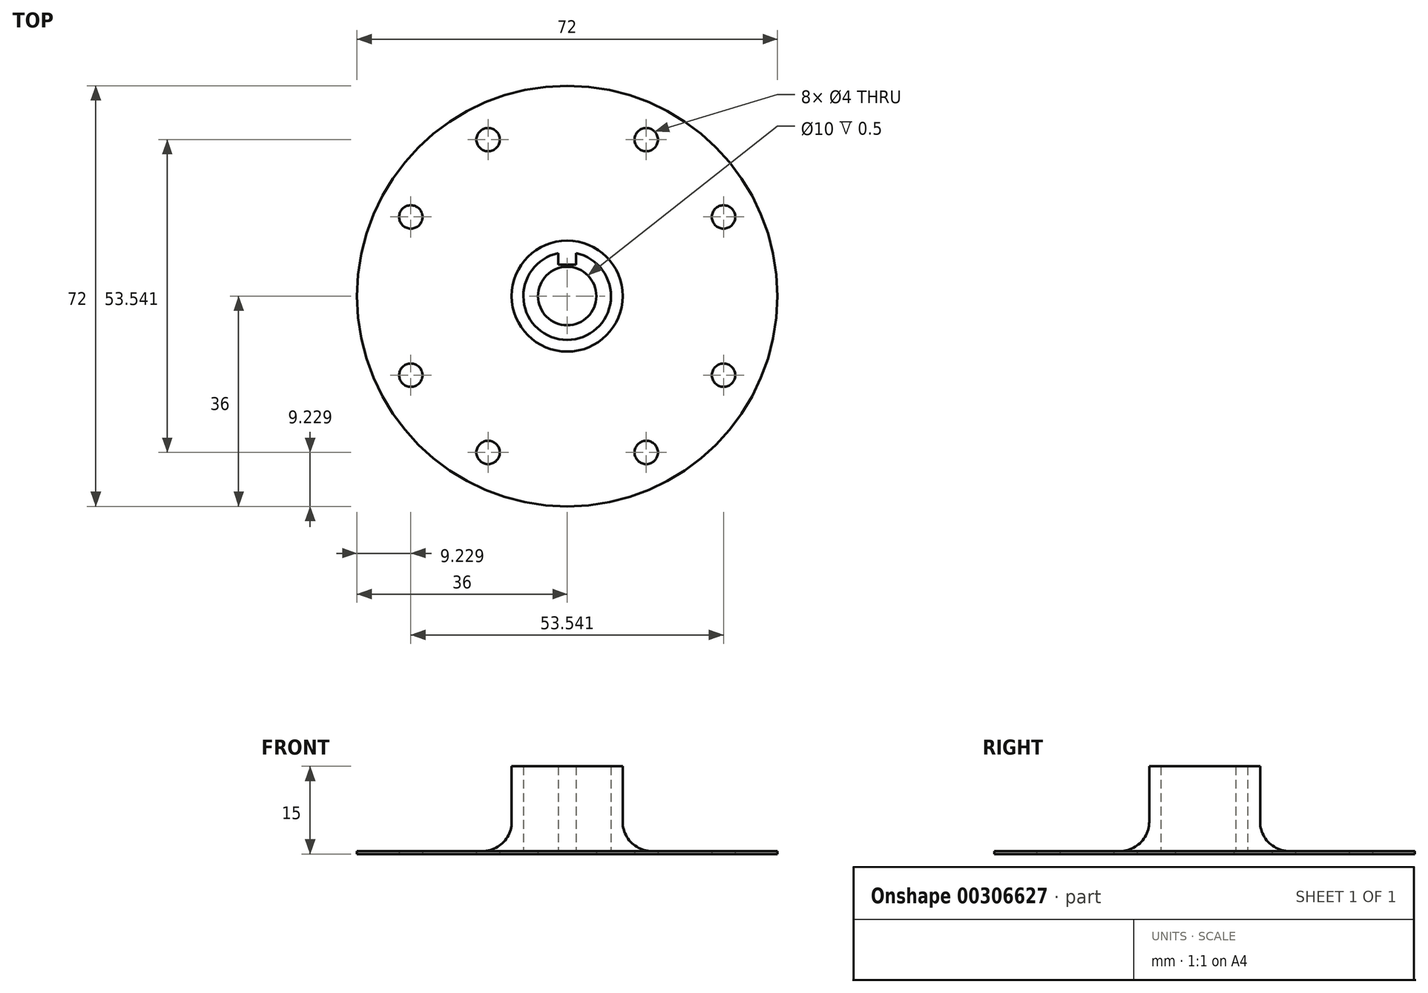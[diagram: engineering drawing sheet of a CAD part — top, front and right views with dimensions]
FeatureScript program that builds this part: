
annotation { "Feature Type Name" : "Feature", "Feature Type Description" : "" }
export const myFeature = defineFeature(function(context is Context, id is Id, definition is map)
    precondition{}
    {
        {
            assignVariable(context, id + "F0", {"name" : "Thicc", "anyValue" : .5});
        }
        {
            var Q0;
            Q0=qCreatedBy(makeId("Top.planeOp"),FACE);
            var sketch = newSketch(context, id + "F1", { "sketchPlane" : qUnion([Q0])});
            skCircle(sketch, "E0", {"center": v(0, 0) * mm, "radius": 7.5 * mm});
            skCircle(sketch, "E1", {"center": v(0, 0) * mm, "radius": 9.5 * mm});
            skLineSegment(sketch, "E2", {"start": v(-1.5, 7.35) * mm, "end": v(-1.5, 5.35) * mm});
            skLineSegment(sketch, "E3", {"start": v(-1.5, 5.35) * mm, "end": v(1.5, 5.35) * mm});
            skLineSegment(sketch, "E4", {"start": v(1.5, 5.35) * mm, "end": v(1.5, 7.35) * mm});
            skPoint(sketch, "E5", {"position": v(0, 5.35) * mm});
            skSolve(sketch);
        }
        {
            var Q0;
            Q0=qCreatedBy(makeId("Top.planeOp"),FACE);
            var sketch = newSketch(context, id + "F2", { "sketchPlane" : qUnion([Q0])});
            skCircle(sketch, "E6", {"center": v(0, 0) * mm, "radius": 2.5 * mm});
            skCircle(sketch, "E7", {"center": v(0, 0) * mm, "radius": 30 * mm});
            skCircle(sketch, "E8", {"center": v(0, 0) * mm, "radius": 6 * mm});
            skCircle(sketch, "E9", {"center": v(0, 0) * mm, "radius": 36 * mm});
            skCircle(sketch, "E10", {"center": v(0, 7.75) * mm, "radius": 1.75 * mm});
            skCircle(sketch, "E11", {"center": v(-7.75, 0) * mm, "radius": 1.75 * mm});
            skCircle(sketch, "E12", {"center": v(0, -7.75) * mm, "radius": 1.75 * mm});
            skCircle(sketch, "E13", {"center": v(7.75, 0) * mm, "radius": 1.75 * mm});
            skPoint(sketch, "E14", {"position": v(-6, 0) * mm});
            skPoint(sketch, "E15", {"position": v(0, 6) * mm});
            skPoint(sketch, "E16", {"position": v(6, 0) * mm});
            skPoint(sketch, "E17", {"position": v(0, -6) * mm});
            skCircle(sketch, "E18", {"center": v(0, 0) * mm, "radius": 4 * mm, "construction": true});
            skLineSegment(sketch, "E19", {"start": v(-24.73, 16.98) * mm, "end": v(16.98, -24.73) * mm, "construction": true});
            skLineSegment(sketch, "E20", {"start": v(-16.98, 24.73) * mm, "end": v(24.73, -16.98) * mm, "construction": true});
            skLineSegment(sketch, "E21", {"start": v(-24.73, -16.98) * mm, "end": v(16.98, 24.73) * mm, "construction": true});
            skLineSegment(sketch, "E22", {"start": v(-16.98, -24.73) * mm, "end": v(24.73, 16.98) * mm, "construction": true});
            skCircle(sketch, "E23", {"center": v(-13.54, 26.77) * mm, "radius": 4 * mm});
            skCircle(sketch, "E24", {"center": v(-26.77, 13.54) * mm, "radius": 4 * mm});
            skCircle(sketch, "E25", {"center": v(-26.77, -13.54) * mm, "radius": 4 * mm});
            skCircle(sketch, "E26", {"center": v(-13.54, -26.77) * mm, "radius": 4 * mm});
            skCircle(sketch, "E27", {"center": v(13.54, -26.77) * mm, "radius": 4 * mm});
            skCircle(sketch, "E28", {"center": v(26.77, -13.54) * mm, "radius": 4 * mm});
            skCircle(sketch, "E29", {"center": v(26.77, 13.54) * mm, "radius": 4 * mm});
            skCircle(sketch, "E30", {"center": v(13.54, 26.77) * mm, "radius": 4 * mm});
            skCircle(sketch, "E31", {"center": v(13.54, -26.77) * mm, "radius": 2 * mm});
            skCircle(sketch, "E32", {"center": v(26.77, -13.54) * mm, "radius": 2 * mm});
            skCircle(sketch, "E33", {"center": v(-13.54, -26.77) * mm, "radius": 2 * mm});
            skCircle(sketch, "E34", {"center": v(-26.77, -13.54) * mm, "radius": 2 * mm});
            skCircle(sketch, "E35", {"center": v(-26.77, 13.54) * mm, "radius": 2 * mm});
            skCircle(sketch, "E36", {"center": v(-13.54, 26.77) * mm, "radius": 2 * mm});
            skCircle(sketch, "E37", {"center": v(13.54, 26.77) * mm, "radius": 2 * mm});
            skCircle(sketch, "E38", {"center": v(26.77, 13.54) * mm, "radius": 2 * mm});
            skSolve(sketch);
        }
        {
            var Q0;
            Q0=makeQuery(id+"F2.imprint","IMPRINT",FACE,{"disambiguationData":[TD([[makeQuery(id+"F2.imprint","IMPRINT",EDGE,{"derivedFrom":sQuery(id+"F2.wireOp",EDGE,"E9")}),1.0]])]});
            var Q1;
            {var subQ9=sQuery(id+"F2.wireOp",EDGE,"E10");Q1=makeQuery(id+"F2.imprint","IMPRINT",FACE,{"disambiguationData":[TD([[makeQuery(id+"F2.imprint","IMPRINT",EDGE,{"derivedFrom":subQ9}),-1.0]])]});}
            var Q2;
            Q2=makeQuery(id+"F2.imprint","IMPRINT",FACE,{"disambiguationData":[TD([[makeQuery(id+"F2.imprint","IMPRINT",EDGE,{"derivedFrom":sQuery(id+"F2.wireOp",EDGE,"E6")}),-1.0]])]});
            var Q3;
            Q3=makeQuery(id+"F2.imprint","IMPRINT",FACE,{"disambiguationData":[TD([[makeQuery(id+"F2.imprint","IMPRINT",EDGE,{"derivedFrom":sQuery(id+"F2.wireOp",EDGE,"E11")}),1.0]])]});
            var Q4;
            Q4=makeQuery(id+"F2.imprint","IMPRINT",FACE,{"disambiguationData":[TD([[makeQuery(id+"F2.imprint","IMPRINT",EDGE,{"derivedFrom":sQuery(id+"F2.wireOp",EDGE,"E13")}),1.0]])]});
            var Q5;
            Q5=makeQuery(id+"F2.imprint","IMPRINT",FACE,{"disambiguationData":[TD([[makeQuery(id+"F2.imprint","IMPRINT",EDGE,{"derivedFrom":sQuery(id+"F2.wireOp",EDGE,"E10")}),1.0]])]});
            var Q6;
            Q6=makeQuery(id+"F2.imprint","IMPRINT",FACE,{"disambiguationData":[TD([[makeQuery(id+"F2.imprint","IMPRINT",EDGE,{"derivedFrom":sQuery(id+"F2.wireOp",EDGE,"E12")}),1.0]])]});
            var Q7;
            {var subQ0=sQuery(id+"F2.wireOp",EDGE,"E26");var subQ1=sQuery(id+"F2.wireOp",EDGE,"E7");var subQ2=makeQuery(id+"F2.imprint","INTERSECT",VERTEX,{"disambiguationData":[OD(0.0)],"derivedFrom":[subQ1,subQ0]});Q7=makeQuery(id+"F2.imprint","IMPRINT",FACE,{"disambiguationData":[TD([[makeQuery(id+"F2.imprint","IMPRINT",EDGE,{"disambiguationData":[TD([[subQ2,-1.0]])],"derivedFrom":subQ1}),-1.0]])]});}
            var Q8;
            {var subQ0=sQuery(id+"F2.wireOp",EDGE,"E26");var subQ1=sQuery(id+"F2.wireOp",EDGE,"E7");var subQ2=makeQuery(id+"F2.imprint","INTERSECT",VERTEX,{"disambiguationData":[OD(0.0)],"derivedFrom":[subQ1,subQ0]});Q8=makeQuery(id+"F2.imprint","IMPRINT",FACE,{"disambiguationData":[TD([[makeQuery(id+"F2.imprint","IMPRINT",EDGE,{"disambiguationData":[TD([[subQ2,-1.0]])],"derivedFrom":subQ1}),1.0]])]});}
            var Q9;
            {var subQ0=sQuery(id+"F2.wireOp",EDGE,"E25");var subQ1=sQuery(id+"F2.wireOp",EDGE,"E7");var subQ2=makeQuery(id+"F2.imprint","INTERSECT",VERTEX,{"disambiguationData":[OD(0.0)],"derivedFrom":[subQ1,subQ0]});Q9=makeQuery(id+"F2.imprint","IMPRINT",FACE,{"disambiguationData":[TD([[makeQuery(id+"F2.imprint","IMPRINT",EDGE,{"disambiguationData":[TD([[subQ2,-1.0]])],"derivedFrom":subQ1}),-1.0]])]});}
            var Q10;
            {var subQ0=sQuery(id+"F2.wireOp",EDGE,"E25");var subQ1=sQuery(id+"F2.wireOp",EDGE,"E7");var subQ2=makeQuery(id+"F2.imprint","INTERSECT",VERTEX,{"disambiguationData":[OD(0.0)],"derivedFrom":[subQ1,subQ0]});Q10=makeQuery(id+"F2.imprint","IMPRINT",FACE,{"disambiguationData":[TD([[makeQuery(id+"F2.imprint","IMPRINT",EDGE,{"disambiguationData":[TD([[subQ2,-1.0]])],"derivedFrom":subQ1}),1.0]])]});}
            var Q11;
            {var subQ0=sQuery(id+"F2.wireOp",EDGE,"E24");var subQ1=sQuery(id+"F2.wireOp",EDGE,"E7");var subQ2=makeQuery(id+"F2.imprint","INTERSECT",VERTEX,{"disambiguationData":[OD(0.0)],"derivedFrom":[subQ1,subQ0]});Q11=makeQuery(id+"F2.imprint","IMPRINT",FACE,{"disambiguationData":[TD([[makeQuery(id+"F2.imprint","IMPRINT",EDGE,{"disambiguationData":[TD([[subQ2,-1.0]])],"derivedFrom":subQ1}),1.0]])]});}
            var Q12;
            {var subQ0=sQuery(id+"F2.wireOp",EDGE,"E24");var subQ1=sQuery(id+"F2.wireOp",EDGE,"E7");var subQ2=makeQuery(id+"F2.imprint","INTERSECT",VERTEX,{"disambiguationData":[OD(0.0)],"derivedFrom":[subQ1,subQ0]});Q12=makeQuery(id+"F2.imprint","IMPRINT",FACE,{"disambiguationData":[TD([[makeQuery(id+"F2.imprint","IMPRINT",EDGE,{"disambiguationData":[TD([[subQ2,-1.0]])],"derivedFrom":subQ1}),-1.0]])]});}
            var Q13;
            {var subQ0=sQuery(id+"F2.wireOp",EDGE,"E23");var subQ1=sQuery(id+"F2.wireOp",EDGE,"E7");var subQ2=makeQuery(id+"F2.imprint","INTERSECT",VERTEX,{"disambiguationData":[OD(0.0)],"derivedFrom":[subQ1,subQ0]});Q13=makeQuery(id+"F2.imprint","IMPRINT",FACE,{"disambiguationData":[TD([[makeQuery(id+"F2.imprint","IMPRINT",EDGE,{"disambiguationData":[TD([[subQ2,-1.0]])],"derivedFrom":subQ1}),-1.0]])]});}
            var Q14;
            {var subQ0=sQuery(id+"F2.wireOp",EDGE,"E23");var subQ1=sQuery(id+"F2.wireOp",EDGE,"E7");var subQ2=makeQuery(id+"F2.imprint","INTERSECT",VERTEX,{"disambiguationData":[OD(0.0)],"derivedFrom":[subQ1,subQ0]});Q14=makeQuery(id+"F2.imprint","IMPRINT",FACE,{"disambiguationData":[TD([[makeQuery(id+"F2.imprint","IMPRINT",EDGE,{"disambiguationData":[TD([[subQ2,-1.0]])],"derivedFrom":subQ1}),1.0]])]});}
            var Q15;
            {var subQ0=sQuery(id+"F2.wireOp",EDGE,"E27");var subQ1=sQuery(id+"F2.wireOp",EDGE,"E7");var subQ2=makeQuery(id+"F2.imprint","INTERSECT",VERTEX,{"disambiguationData":[OD(0.0)],"derivedFrom":[subQ1,subQ0]});Q15=makeQuery(id+"F2.imprint","IMPRINT",FACE,{"disambiguationData":[TD([[makeQuery(id+"F2.imprint","IMPRINT",EDGE,{"disambiguationData":[TD([[subQ2,-1.0]])],"derivedFrom":subQ1}),-1.0]])]});}
            var Q16;
            {var subQ0=sQuery(id+"F2.wireOp",EDGE,"E27");var subQ1=sQuery(id+"F2.wireOp",EDGE,"E7");var subQ2=makeQuery(id+"F2.imprint","INTERSECT",VERTEX,{"disambiguationData":[OD(0.0)],"derivedFrom":[subQ1,subQ0]});Q16=makeQuery(id+"F2.imprint","IMPRINT",FACE,{"disambiguationData":[TD([[makeQuery(id+"F2.imprint","IMPRINT",EDGE,{"disambiguationData":[TD([[subQ2,-1.0]])],"derivedFrom":subQ1}),1.0]])]});}
            var Q17;
            {var subQ0=sQuery(id+"F2.wireOp",EDGE,"E28");var subQ1=sQuery(id+"F2.wireOp",EDGE,"E7");var subQ2=makeQuery(id+"F2.imprint","INTERSECT",VERTEX,{"disambiguationData":[OD(0.0)],"derivedFrom":[subQ1,subQ0]});Q17=makeQuery(id+"F2.imprint","IMPRINT",FACE,{"disambiguationData":[TD([[makeQuery(id+"F2.imprint","IMPRINT",EDGE,{"disambiguationData":[TD([[subQ2,-1.0]])],"derivedFrom":subQ1}),-1.0]])]});}
            var Q18;
            {var subQ0=sQuery(id+"F2.wireOp",EDGE,"E28");var subQ1=sQuery(id+"F2.wireOp",EDGE,"E7");var subQ2=makeQuery(id+"F2.imprint","INTERSECT",VERTEX,{"disambiguationData":[OD(0.0)],"derivedFrom":[subQ1,subQ0]});Q18=makeQuery(id+"F2.imprint","IMPRINT",FACE,{"disambiguationData":[TD([[makeQuery(id+"F2.imprint","IMPRINT",EDGE,{"disambiguationData":[TD([[subQ2,-1.0]])],"derivedFrom":subQ1}),1.0]])]});}
            var Q19;
            {var subQ0=sQuery(id+"F2.wireOp",EDGE,"E38");var subQ1=sQuery(id+"F2.wireOp",EDGE,"E7");var subQ2=makeQuery(id+"F2.imprint","INTERSECT",VERTEX,{"disambiguationData":[OD(0.0)],"derivedFrom":[subQ1,subQ0]});Q19=makeQuery(id+"F2.imprint","IMPRINT",FACE,{"disambiguationData":[TD([[makeQuery(id+"F2.imprint","IMPRINT",EDGE,{"disambiguationData":[TD([[subQ2,1.0]])],"derivedFrom":subQ1}),-1.0]])]});}
            var Q20;
            {var subQ0=sQuery(id+"F2.wireOp",EDGE,"E38");var subQ1=sQuery(id+"F2.wireOp",EDGE,"E7");var subQ2=makeQuery(id+"F2.imprint","INTERSECT",VERTEX,{"disambiguationData":[OD(0.0)],"derivedFrom":[subQ1,subQ0]});Q20=makeQuery(id+"F2.imprint","IMPRINT",FACE,{"disambiguationData":[TD([[makeQuery(id+"F2.imprint","IMPRINT",EDGE,{"disambiguationData":[TD([[subQ2,1.0]])],"derivedFrom":subQ1}),1.0]])]});}
            var Q21;
            {var subQ0=sQuery(id+"F2.wireOp",EDGE,"E30");var subQ1=sQuery(id+"F2.wireOp",EDGE,"E7");var subQ2=makeQuery(id+"F2.imprint","INTERSECT",VERTEX,{"disambiguationData":[OD(0.0)],"derivedFrom":[subQ1,subQ0]});Q21=makeQuery(id+"F2.imprint","IMPRINT",FACE,{"disambiguationData":[TD([[makeQuery(id+"F2.imprint","IMPRINT",EDGE,{"disambiguationData":[TD([[subQ2,-1.0]])],"derivedFrom":subQ1}),-1.0]])]});}
            var Q22;
            {var subQ0=sQuery(id+"F2.wireOp",EDGE,"E30");var subQ1=sQuery(id+"F2.wireOp",EDGE,"E7");var subQ2=makeQuery(id+"F2.imprint","INTERSECT",VERTEX,{"disambiguationData":[OD(0.0)],"derivedFrom":[subQ1,subQ0]});Q22=makeQuery(id+"F2.imprint","IMPRINT",FACE,{"disambiguationData":[TD([[makeQuery(id+"F2.imprint","IMPRINT",EDGE,{"disambiguationData":[TD([[subQ2,-1.0]])],"derivedFrom":subQ1}),1.0]])]});}
            extrude(context, id + "F3", {"entities" : qUnion([Q0, Q1, Q2, Q3, Q4, Q5, Q6, Q7, Q8, Q9, Q10, Q11, Q12, Q13, Q14, Q15, Q16, Q17, Q18, Q19, Q20, Q21, Q22]), "depth" : (getVariable(context, 'Thicc')) * mm});
        }
        {
            var Q0;
            Q0=makeQuery(id+"F1.imprint","IMPRINT",FACE,{"disambiguationData":[TD([[makeQuery(id+"F1.imprint","IMPRINT",EDGE,{"derivedFrom":sQuery(id+"F1.wireOp",EDGE,"E1")}),1.0]])]});
            var Q1;
            {var subQ0=sQuery(id+"F1.wireOp",EDGE,"E2");Q1=makeQuery(id+"F1.imprint","IMPRINT",FACE,{"disambiguationData":[TD([[makeQuery(id+"F1.imprint","IMPRINT",EDGE,{"derivedFrom":subQ0}),1.0]])]});}
            extrude(context, id + "F4", {"entities" : qUnion([Q0, Q1]), "operationType" : NewBodyOperationType.ADD, "depth" : 15 * mm});
        }
        {
            var Q0;
            Q0=makeQuery(id+"F4.boolean.opBoolean","INTERSECT",EDGE,{"derivedFrom":[makeQuery(id+"F3.opExtrude","CAP_FACE",FACE,{"disambiguationData":[OSD([sQuery(id+"F2.wireOp",EDGE,"E6"),sQuery(id+"F2.wireOp",EDGE,"E9"),sQuery(id+"F2.wireOp",EDGE,"E23"),sQuery(id+"F2.wireOp",EDGE,"E24"),sQuery(id+"F2.wireOp",EDGE,"E25"),sQuery(id+"F2.wireOp",EDGE,"E26"),sQuery(id+"F2.wireOp",EDGE,"E27"),sQuery(id+"F2.wireOp",EDGE,"E28"),sQuery(id+"F2.wireOp",EDGE,"E29"),sQuery(id+"F2.wireOp",EDGE,"E30")])],"isStart":false}),makeQuery(id+"F4.opExtrude","SWEPT_FACE",FACE,{"disambiguationData":[OSD([sQuery(id+"F1.wireOp",EDGE,"E1")])]})]});
            fillet(context, id + "F5", {"entities" : qUnion([Q0]), "radius" : 5 * mm, "tangentPropagation" : true, "allowEdgeOverflow" : false});
        }
        {
            var Q0;
            Q0=sQuery(id+"F2.wireOp",VERTEX,"E9.center");
            var Q1;
            Q1=makeQuery(id+"F3.opExtrude","SWEPT_BODY",BODY,{"disambiguationData":[OSD([sQuery(id+"F2.wireOp",EDGE,"E6"),sQuery(id+"F2.wireOp",EDGE,"E9"),sQuery(id+"F2.wireOp",EDGE,"E23"),sQuery(id+"F2.wireOp",EDGE,"E24"),sQuery(id+"F2.wireOp",EDGE,"E25"),sQuery(id+"F2.wireOp",EDGE,"E26"),sQuery(id+"F2.wireOp",EDGE,"E27"),sQuery(id+"F2.wireOp",EDGE,"E28"),sQuery(id+"F2.wireOp",EDGE,"E29"),sQuery(id+"F2.wireOp",EDGE,"E30")])]});
            hole(context, id + "F6", {"style" : HoleStyle.SIMPLE, "endStyle" : HoleEndStyle.BLIND, "oppositeDirection" : true, "holeDiameter" : 10 * mm, "holeDepth" : 3.5 * mm, "tappedDepth" : 12 * mm, "tapClearance" : 3, "startFromSketch" : true, "locations" : qUnion([Q0]), "scope" : qUnion([Q1])});
        }
    });
